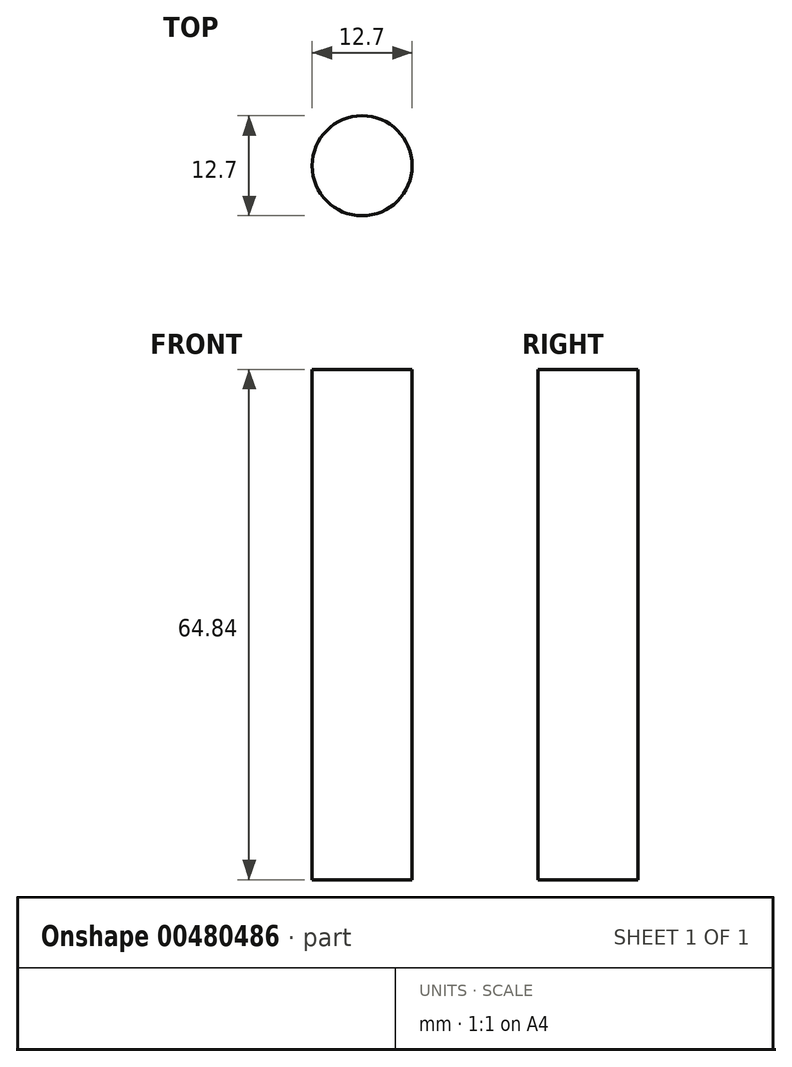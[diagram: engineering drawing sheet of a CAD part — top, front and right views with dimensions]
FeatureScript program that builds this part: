
annotation { "Feature Type Name" : "Feature", "Feature Type Description" : "" }
export const myFeature = defineFeature(function(context is Context, id is Id, definition is map)
    precondition{}
    {
        {
            var Q0;
            Q0=qCreatedBy(makeId("Top.planeOp"),FACE);
            var sketch = newSketch(context, id + "F0", { "sketchPlane" : qUnion([Q0])});
            skCircle(sketch, "E0", {"center": v(0, 0) * mm, "radius": 6.35 * mm});
            skSolve(sketch);
        }
        {
            var Q0;
            Q0 = qSketchRegion(id + "F0", true);
            extrude(context, id + "F1", {"entities" : qUnion([Q0]), "depth" : 64.84 * mm});
        }
    });
